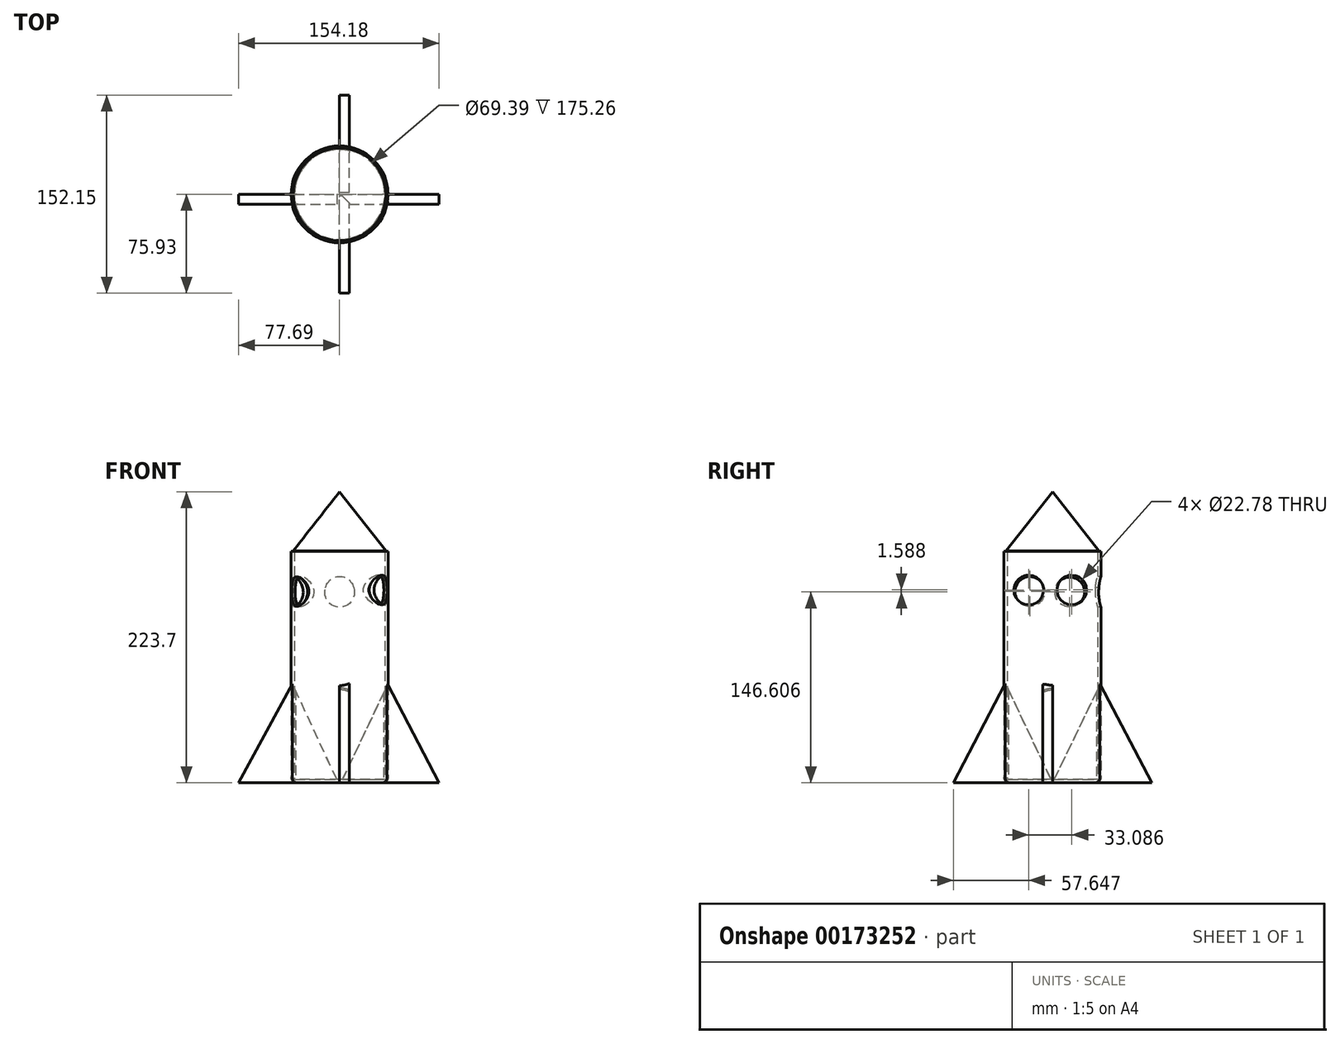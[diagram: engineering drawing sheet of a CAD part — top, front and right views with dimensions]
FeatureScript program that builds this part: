
annotation { "Feature Type Name" : "Feature", "Feature Type Description" : "" }
export const myFeature = defineFeature(function(context is Context, id is Id, definition is map)
    precondition{}
    {
        {
            var Q0;
            Q0=qCreatedBy(makeId("Top.planeOp"),FACE);
            var sketch = newSketch(context, id + "F0", { "sketchPlane" : qUnion([Q0])});
            skCircle(sketch, "E0", {"center": v(0, 0) * mm, "radius": 37.24 * mm});
            skSolve(sketch);
        }
        {
            var Q0;
            Q0 = qSketchRegion(id + "F0", true);
            extrude(context, id + "F1", {"entities" : qUnion([Q0]), "depth" : 177.8 * mm});
        }
        {
            var Q0;
            Q0=makeQuery(id+"F1.opExtrude","CAP_FACE",FACE,{"disambiguationData":[OSD([sQuery(id+"F0.wireOp",EDGE,"E0")])],"isStart":false});
            shell(context, id + "F2", {"entities" : qUnion([Q0]), "thickness" : 2.54 * mm});
        }
        {
            var Q0;
            Q0=makeQuery(id+"F1.opExtrude","CAP_EDGE",EDGE,{"disambiguationData":[OSD([sQuery(id+"F0.wireOp",EDGE,"E0")])],"isStart":true});
            fillet(context, id + "F3", {"entities" : qUnion([Q0]), "radius" : 4.3 * mm, "tangentPropagation" : true, "rho" : 0.5, "crossSection" : FilletCrossSection.CONIC, "allowEdgeOverflow" : false});
        }
        {
            var Q0;
            Q0=qCreatedBy(makeId("Front.planeOp"),FACE);
            var sketch = newSketch(context, id + "F4", { "sketchPlane" : qUnion([Q0])});
            skLineSegment(sketch, "E1", {"start": v(36.86, 75.68) * mm, "end": v(76.5, 0) * mm});
            skLineSegment(sketch, "E2", {"start": v(76.5, 0) * mm, "end": v(0, 0) * mm});
            skLineSegment(sketch, "E3", {"start": v(-36.32, 76.26) * mm, "end": v(-77.69, 0) * mm});
            skLineSegment(sketch, "E4", {"start": v(-77.69, 0) * mm, "end": v(0, 0) * mm});
            skLineSegment(sketch, "E5", {"start": v(36.86, 75.68) * mm, "end": v(0, -2.14) * mm});
            skLineSegment(sketch, "E6", {"start": v(0, -2.14) * mm, "end": v(-36.32, 76.26) * mm});
            skSolve(sketch);
        }
        {
            var Q0;
            {var subQ0=sQuery(id+"F4.wireOp",EDGE,"E1");Q0=makeQuery(id+"F4.imprint","IMPRINT",FACE,{"disambiguationData":[TD([[makeQuery(id+"F4.imprint","IMPRINT",EDGE,{"derivedFrom":subQ0}),-1.0]])]});}
            var Q1;
            {var subQ0=sQuery(id+"F4.wireOp",EDGE,"E3");Q1=makeQuery(id+"F4.imprint","IMPRINT",FACE,{"disambiguationData":[TD([[makeQuery(id+"F4.imprint","IMPRINT",EDGE,{"derivedFrom":subQ0}),1.0]])]});}
            extrude(context, id + "F5", {"entities" : qUnion([Q0, Q1]), "operationType" : NewBodyOperationType.ADD, "depth" : 7.62 * mm});
        }
        {
            var Q0;
            Q0=qCreatedBy(makeId("Right.planeOp"),FACE);
            var sketch = newSketch(context, id + "F6", { "sketchPlane" : qUnion([Q0])});
            skLineSegment(sketch, "E7", {"start": v(36.6, 75.68) * mm, "end": v(76.22, 0) * mm});
            skLineSegment(sketch, "E8", {"start": v(76.22, 0) * mm, "end": v(0, 0) * mm});
            skLineSegment(sketch, "E9", {"start": v(0, 0) * mm, "end": v(-75.93, 0) * mm});
            skLineSegment(sketch, "E10", {"start": v(-75.93, 0) * mm, "end": v(-36.3, 76.54) * mm});
            skLineSegment(sketch, "E11", {"start": v(-36.3, 76.54) * mm, "end": v(0, 0) * mm});
            skLineSegment(sketch, "E12", {"start": v(36.6, 75.68) * mm, "end": v(0, 0) * mm});
            skSolve(sketch);
        }
        {
            var Q0;
            Q0=makeQuery(id+"F6.imprint","IMPRINT",FACE,{"disambiguationData":[TD([[makeQuery(id+"F6.imprint","IMPRINT",EDGE,{"derivedFrom":sQuery(id+"F6.wireOp",EDGE,"E7")}),-1.0]])]});
            var Q1;
            Q1=makeQuery(id+"F6.imprint","IMPRINT",FACE,{"disambiguationData":[TD([[makeQuery(id+"F6.imprint","IMPRINT",EDGE,{"derivedFrom":sQuery(id+"F6.wireOp",EDGE,"E9")}),-1.0]])]});
            extrude(context, id + "F7", {"entities" : qUnion([Q0, Q1]), "operationType" : NewBodyOperationType.ADD, "depth" : 7.62 * mm});
        }
        {
            var Q0;
            Q0=qCreatedBy(makeId("Right.planeOp"),FACE);
            var sketch = newSketch(context, id + "F8", { "sketchPlane" : qUnion([Q0])});
            skLineSegment(sketch, "E13", {"start": v(0, 177.43) * mm, "end": v(0, 223.7) * mm});
            skLineSegment(sketch, "E14", {"start": v(0, 223.7) * mm, "end": v(35.66, 178.13) * mm});
            skLineSegment(sketch, "E15", {"start": v(35.66, 178.13) * mm, "end": v(0, 177.43) * mm});
            skSolve(sketch);
        }
        {
            var Q0;
            Q0=makeQuery(id+"F8.imprint","IMPRINT",FACE,{"disambiguationData":[TD([[makeQuery(id+"F8.imprint","IMPRINT",EDGE,{"derivedFrom":sQuery(id+"F8.wireOp",EDGE,"E13")}),-1.0]])]});
            var Q1;
            Q1=sQuery(id+"F8.wireOp",EDGE,"E13");
            revolve(context, id + "F9", {"entities" : qUnion([Q0]), "axis" : qUnion([Q1]), "revolveType" : RevolveType.FULL});
        }
        {
            var Q0;
            Q0=qCreatedBy(makeId("Right.planeOp"),FACE);
            var sketch = newSketch(context, id + "F10", { "sketchPlane" : qUnion([Q0])});
            skCircle(sketch, "E16", {"center": v(14.8, 148.2) * mm, "radius": 11.39 * mm});
            skCircle(sketch, "E17", {"center": v(-18.28, 148.12) * mm, "radius": 11.36 * mm});
            skSolve(sketch);
        }
        {
            var Q0;
            Q0=sQuery(id+"F10.wireOp",VERTEX,"E16.center");
            var Q1;
            Q1=sQuery(id+"F10.wireOp",VERTEX,"E17.center");
            var Q2;
            Q2=makeQuery(id+"F1.opExtrude","SWEPT_BODY",BODY,{"disambiguationData":[OSD([sQuery(id+"F0.wireOp",EDGE,"E0")])]});
            hole(context, id + "F11", {"style" : HoleStyle.SIMPLE, "endStyle" : HoleEndStyle.THROUGH, "oppositeDirection" : true, "holeDiameter" : 22.78 * mm, "locations" : qUnion([Q0, Q1]), "scope" : qUnion([Q2]), "isTappedThrough" : true});
        }
        {
            var Q0;
            Q0=qCreatedBy(makeId("Right.planeOp"),FACE);
            var sketch = newSketch(context, id + "F12", { "sketchPlane" : qUnion([Q0])});
            skCircle(sketch, "E18", {"center": v(13.23, 146.6) * mm, "radius": 11.63 * mm});
            skCircle(sketch, "E19", {"center": v(-17.43, 146.99) * mm, "radius": 12.46 * mm});
            skSolve(sketch);
        }
        {
            var Q0;
            Q0=sQuery(id+"F12.wireOp",VERTEX,"E18.center");
            var Q1;
            Q1=sQuery(id+"F12.wireOp",VERTEX,"E19.center");
            var Q2;
            Q2=makeQuery(id+"F1.opExtrude","SWEPT_BODY",BODY,{"disambiguationData":[OSD([sQuery(id+"F0.wireOp",EDGE,"E0")])]});
            hole(context, id + "F13", {"style" : HoleStyle.SIMPLE, "endStyle" : HoleEndStyle.THROUGH, "holeDiameter" : 22.78 * mm, "locations" : qUnion([Q0, Q1]), "scope" : qUnion([Q2]), "isTappedThrough" : true});
        }
        {
            var Q0;
            Q0=qCreatedBy(makeId("Front.planeOp"),FACE);
            var sketch = newSketch(context, id + "F14", { "sketchPlane" : qUnion([Q0])});
            skCircle(sketch, "E20", {"center": v(0, 146.23) * mm, "radius": 12.32 * mm});
            skCircle(sketch, "E21", {"center": v(0, 146.23) * mm, "radius": 12.74 * mm});
            skSolve(sketch);
        }
        {
            var Q0;
            Q0=sQuery(id+"F14.wireOp",VERTEX,"E20.center");
            var Q1;
            Q1=makeQuery(id+"F1.opExtrude","SWEPT_BODY",BODY,{"disambiguationData":[OSD([sQuery(id+"F0.wireOp",EDGE,"E0")])]});
            hole(context, id + "F15", {"style" : HoleStyle.SIMPLE, "endStyle" : HoleEndStyle.THROUGH, "holeDiameter" : 22.78 * mm, "locations" : qUnion([Q0]), "scope" : qUnion([Q1]), "isTappedThrough" : true});
        }
        {
            var Q0;
            Q0=qCreatedBy(makeId("Front.planeOp"),FACE);
            var sketch = newSketch(context, id + "F16", { "sketchPlane" : qUnion([Q0])});
            skCircle(sketch, "E22", {"center": v(0, 147.52) * mm, "radius": 11.08 * mm});
            skSolve(sketch);
        }
        {
            var Q0;
            Q0=sQuery(id+"F16.wireOp",VERTEX,"E22.center");
            var Q1;
            Q1=makeQuery(id+"F1.opExtrude","SWEPT_BODY",BODY,{"disambiguationData":[OSD([sQuery(id+"F0.wireOp",EDGE,"E0")])]});
            hole(context, id + "F17", {"style" : HoleStyle.SIMPLE, "endStyle" : HoleEndStyle.THROUGH, "holeDiameter" : 22.1 * mm, "locations" : qUnion([Q0]), "scope" : qUnion([Q1]), "isTappedThrough" : true});
        }
    });
